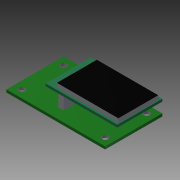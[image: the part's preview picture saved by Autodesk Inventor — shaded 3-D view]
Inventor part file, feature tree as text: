
AUTODESK INVENTOR PART (.ipt)
format: ipt  version: 2015 (Build 190159000, 159)  size: 139,776 bytes
history: native  units: mm
features: extrude x6, sketch x6, other x1
ambient origin geometry x8: Origin, YZ Plane, XZ Plane, XY Plane, X Axis, Y Axis, Z Axis, Center Point
bodies: Body1 (feature_tree)
feature tree (13):
  other  "ソリッド1"
  extrude  "押し出し1"  Depth=48.26mm
  extrude  "押し出し2"  Depth=27.94mm
  extrude  "押し出し3"  Depth=1.3mm TaperAngle=0.0deg
  extrude  "押し出し4"  Depth=3.81mm
  extrude  "押し出し5"  Depth=3.81mm
  extrude  "押し出し6"  Depth=3.81mm
  sketch  "スケッチ1"
  sketch  "スケッチ2"
  sketch  "スケッチ3"
  sketch  "スケッチ4"
  sketch  "スケッチ5"
  sketch  "スケッチ6"
